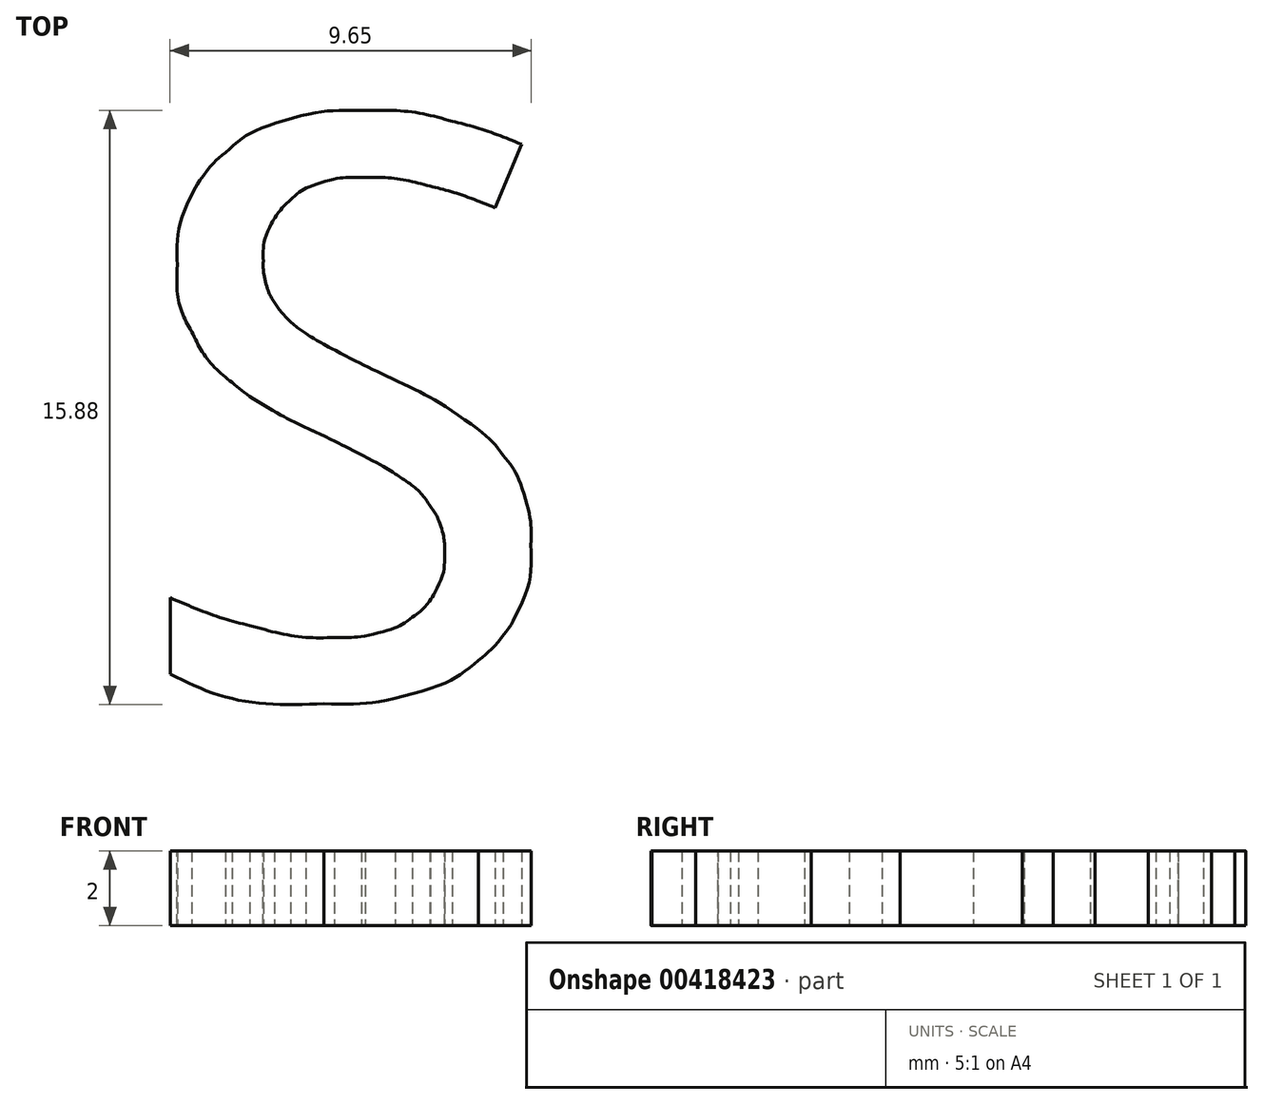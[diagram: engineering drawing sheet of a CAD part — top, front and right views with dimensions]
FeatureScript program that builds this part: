
annotation { "Feature Type Name" : "Feature", "Feature Type Description" : "" }
export const myFeature = defineFeature(function(context is Context, id is Id, definition is map)
    precondition{}
    {
        {
            var Q0;
            Q0=qCreatedBy(makeId("Top.planeOp"),FACE);
            var sketch = newSketch(context, id + "F0", { "sketchPlane" : qUnion([Q0])});
            skFitSpline(sketch, "E0.0", {"points": [v(-4.55, 3.44) * mm, v(-4.55, 4.1) * mm, v(-4.44, 4.68) * mm, v(-4.12, 5.42) * mm, v(-3.99, 5.65) * mm, v(-3.67, 6.08) * mm, v(-3.49, 6.27) * mm, v(-3.27, 6.46) * mm]});
            skFitSpline(sketch, "E0.1", {"points": [v(-4.17, 1.67) * mm, v(-4.42, 2.16) * mm, v(-4.55, 2.74) * mm, v(-4.55, 3.44) * mm]});
            skFitSpline(sketch, "E0.2", {"points": [v(-3.27, 6.46) * mm, v(-2.84, 6.82) * mm, v(-2.32, 7.1) * mm, v(-1.08, 7.48) * mm, v(-0.35, 7.58) * mm, v(0.47, 7.58) * mm]});
            skFitSpline(sketch, "E0.3", {"points": [v(0.47, 7.58) * mm, v(1.29, 7.58) * mm, v(2.06, 7.48) * mm, v(2.79, 7.3) * mm]});
            skFitSpline(sketch, "E0.4", {"points": [v(2.79, 7.3) * mm, v(3.38, 7.14) * mm, v(4, 6.93) * mm, v(4.64, 6.68) * mm]});
            skLineSegment(sketch, "E0.5", {"start": v(4.64, 6.68) * mm, "end": v(3.94, 4.98) * mm});
            skFitSpline(sketch, "E0.6", {"points": [v(3.94, 4.98) * mm, v(3.27, 5.24) * mm, v(2.7, 5.43) * mm, v(2.2, 5.56) * mm]});
            skFitSpline(sketch, "E0.7", {"points": [v(2.2, 5.56) * mm, v(1.58, 5.7) * mm, v(0.97, 5.79) * mm, v(0.36, 5.79) * mm]});
            skFitSpline(sketch, "E0.8", {"points": [v(0.36, 5.79) * mm, v(-0.01, 5.79) * mm, v(-0.36, 5.74) * mm, v(-1, 5.55) * mm, v(-1.29, 5.4) * mm, v(-1.53, 5.19) * mm]});
            skFitSpline(sketch, "E0.9", {"points": [v(-1.53, 5.19) * mm, v(-1.65, 5.09) * mm, v(-1.75, 4.97) * mm, v(-1.94, 4.73) * mm, v(-2.01, 4.6) * mm, v(-2.2, 4.18) * mm, v(-2.26, 3.87) * mm, v(-2.26, 3.56) * mm]});
            skFitSpline(sketch, "E0.10", {"points": [v(-2.26, 3.56) * mm, v(-2.26, 3.36) * mm, v(-2.23, 3.16) * mm, v(-2.13, 2.8) * mm, v(-2.06, 2.61) * mm, v(-1.96, 2.45) * mm]});
            skFitSpline(sketch, "E0.11", {"points": [v(-3.09, 0.31) * mm, v(-3.54, 0.7) * mm, v(-3.9, 1.15) * mm, v(-4.17, 1.67) * mm]});
            skFitSpline(sketch, "E0.12", {"points": [v(-1.96, 2.45) * mm, v(-1.86, 2.3) * mm, v(-1.73, 2.14) * mm, v(-1.45, 1.87) * mm, v(-1.3, 1.74) * mm, v(-1.11, 1.62) * mm]});
            skFitSpline(sketch, "E0.13", {"points": [v(-1.11, 1.62) * mm, v(-1.02, 1.55) * mm, v(-0.9, 1.48) * mm, v(-0.62, 1.32) * mm, v(-0.46, 1.23) * mm, v(0.11, 0.94) * mm, v(0.6, 0.7) * mm, v(1.18, 0.42) * mm]});
            skFitSpline(sketch, "E0.14", {"points": [v(-0.95, -0.97) * mm, v(-0.95, -0.97) * mm, v(-0.95, -0.97) * mm, v(-0.95, -0.97) * mm, v(-1.44, -0.74) * mm, v(-1.86, -0.52) * mm, v(-2.58, -0.09) * mm, v(-2.87, 0.12) * mm, v(-3.09, 0.31) * mm]});
            skFitSpline(sketch, "E0.15", {"points": [v(1.18, 0.42) * mm, v(1.93, 0.06) * mm, v(2.55, -0.3) * mm, v(3.55, -1) * mm, v(3.91, -1.33) * mm, v(4.15, -1.64) * mm]});
            skFitSpline(sketch, "E0.16", {"points": [v(1.26, -2.13) * mm, v(1.06, -2) * mm, v(0.78, -1.84) * mm, v(0.05, -1.46) * mm, v(-0.4, -1.23) * mm, v(-0.95, -0.97) * mm, v(-0.95, -0.97) * mm, v(-0.95, -0.97) * mm, v(-0.95, -0.97) * mm]});
            skFitSpline(sketch, "E0.17", {"points": [v(2.2, -3) * mm, v(1.97, -2.67) * mm, v(1.65, -2.4) * mm, v(1.26, -2.13) * mm]});
            skFitSpline(sketch, "E0.18", {"points": [v(2.58, -4.2) * mm, v(2.58, -3.98) * mm, v(2.55, -3.77) * mm, v(2.43, -3.36) * mm, v(2.33, -3.17) * mm, v(2.2, -3) * mm]});
            skFitSpline(sketch, "E0.19", {"points": [v(4.15, -1.64) * mm, v(4.4, -1.96) * mm, v(4.58, -2.3) * mm, v(4.83, -3.1) * mm, v(4.9, -3.53) * mm, v(4.9, -4.02) * mm]});
            skFitSpline(sketch, "E0.20", {"points": [v(4.9, -4.02) * mm, v(4.9, -4.7) * mm, v(4.77, -5.28) * mm, v(4.42, -6.04) * mm, v(4.28, -6.28) * mm, v(3.93, -6.71) * mm, v(3.73, -6.92) * mm, v(3.5, -7.1) * mm]});
            skFitSpline(sketch, "E0.21", {"points": [v(1.73, -5.96) * mm, v(1.87, -5.86) * mm, v(2, -5.75) * mm, v(2.21, -5.49) * mm, v(2.3, -5.35) * mm, v(2.52, -4.89) * mm, v(2.58, -4.55) * mm, v(2.58, -4.2) * mm]});
            skFitSpline(sketch, "E0.22", {"points": [v(-0.36, -6.5) * mm, v(0.06, -6.5) * mm, v(0.44, -6.46) * mm, v(1.14, -6.29) * mm, v(1.46, -6.15) * mm, v(1.73, -5.96) * mm]});
            skFitSpline(sketch, "E0.23", {"points": [v(3.5, -7.1) * mm, v(3.02, -7.49) * mm, v(2.45, -7.78) * mm, v(1.08, -8.17) * mm, v(0.28, -8.27) * mm, v(-0.63, -8.27) * mm]});
            skFitSpline(sketch, "E0.24", {"points": [v(-2.62, -6.18) * mm, v(-1.81, -6.4) * mm, v(-1.06, -6.5) * mm, v(-0.36, -6.5) * mm]});
            skFitSpline(sketch, "E0.25", {"points": [v(-4.75, -5.44) * mm, v(-3.95, -5.77) * mm, v(-3.24, -6.02) * mm, v(-2.62, -6.18) * mm]});
            skLineSegment(sketch, "E0.26", {"start": v(-4.75, -7.48) * mm, "end": v(-4.75, -5.44) * mm});
            skFitSpline(sketch, "E0.27", {"points": [v(-0.63, -8.27) * mm, v(-2.19, -8.27) * mm, v(-3.55, -8) * mm, v(-4.75, -7.48) * mm]});
            skSolve(sketch);
        }
        {
            var Q0;
            Q0=makeQuery(id+"F0.imprint","IMPRINT",FACE,{"disambiguationData":[TD([[makeQuery(id+"F0.imprint","IMPRINT",EDGE,{"derivedFrom":sQuery(id+"F0.wireOp",EDGE,"E0.0")}),-1.0]])]});
            extrude(context, id + "F1", {"entities" : qUnion([Q0]), "depth" : 2 * mm});
        }
    });
